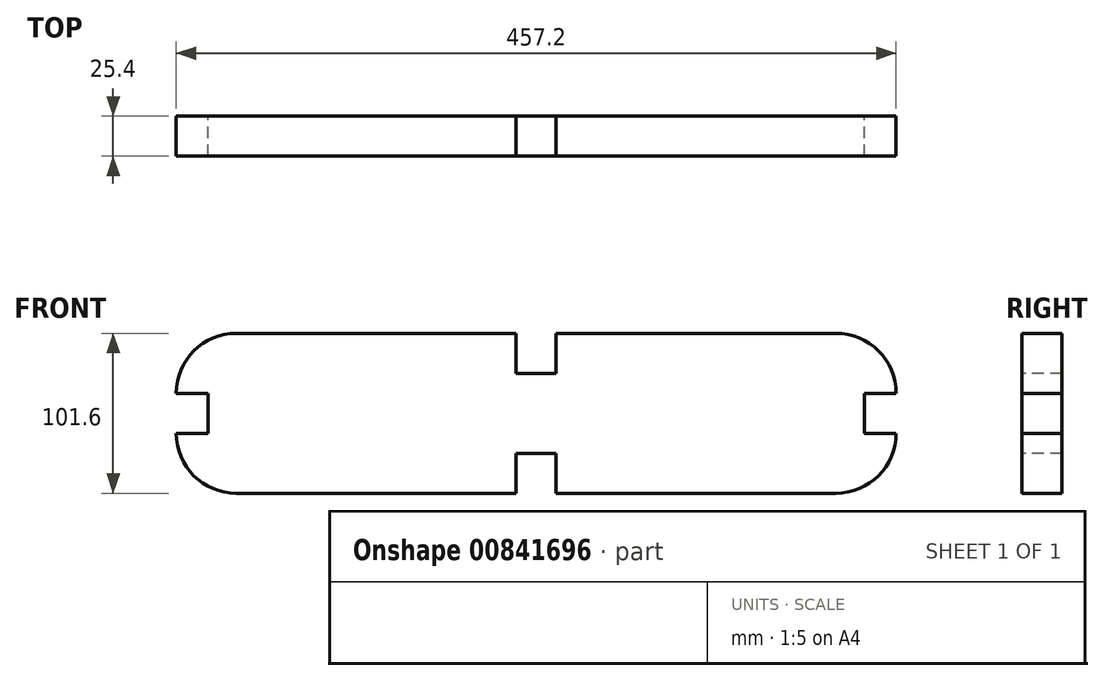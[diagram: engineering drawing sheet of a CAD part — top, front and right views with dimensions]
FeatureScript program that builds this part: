
annotation { "Feature Type Name" : "Feature", "Feature Type Description" : "" }
export const myFeature = defineFeature(function(context is Context, id is Id, definition is map)
    precondition{}
    {
        {
            var Q0;
            Q0=qCreatedBy(makeId("Front.planeOp"),FACE);
            var sketch = newSketch(context, id + "F0", { "sketchPlane" : qUnion([Q0])});
            skLineSegment(sketch, "E0", {"start": v(0, 0) * mm, "end": v(-228.6, 0) * mm, "construction": true});
            skLineSegment(sketch, "E1", {"start": v(0, 0) * mm, "end": v(228.6, 0) * mm, "construction": true});
            skLineSegment(sketch, "E2", {"start": v(0, 0) * mm, "end": v(0, 50.8) * mm, "construction": true});
            skLineSegment(sketch, "E3", {"start": v(0, 0) * mm, "end": v(0, -50.8) * mm, "construction": true});
            skLineSegment(sketch, "E4", {"start": v(0, 50.8) * mm, "end": v(-190.5, 50.8) * mm});
            skLineSegment(sketch, "E5", {"start": v(0, -50.8) * mm, "end": v(-190.5, -50.8) * mm});
            skLineSegment(sketch, "E6", {"start": v(-208.36, 0) * mm, "end": v(-208.36, 12.7) * mm});
            skLineSegment(sketch, "E7", {"start": v(-208.36, 0) * mm, "end": v(-208.36, -12.7) * mm});
            skLineSegment(sketch, "E8", {"start": v(-208.36, 12.7) * mm, "end": v(-228.6, 12.7) * mm});
            skLineSegment(sketch, "E9", {"start": v(-208.36, -12.7) * mm, "end": v(-228.6, -12.7) * mm});
            skLineSegment(sketch, "E10.MirrorCS", {"start": v(0, 50.8) * mm, "end": v(190.5, 50.8) * mm});
            skLineSegment(sketch, "E11.MirrorCS", {"start": v(208.36, 12.7) * mm, "end": v(228.6, 12.7) * mm});
            skLineSegment(sketch, "E12.MirrorCS", {"start": v(208.36, 0) * mm, "end": v(208.36, 12.7) * mm});
            skLineSegment(sketch, "E13.MirrorCS", {"start": v(208.36, 0) * mm, "end": v(208.36, -12.7) * mm});
            skLineSegment(sketch, "E14.MirrorCS", {"start": v(208.36, -12.7) * mm, "end": v(228.6, -12.7) * mm});
            skLineSegment(sketch, "E15.MirrorCS", {"start": v(0, -50.8) * mm, "end": v(190.5, -50.8) * mm});
            skLineSegment(sketch, "E16", {"start": v(-228.6, 12.7) * mm, "end": v(-228.6, 0) * mm, "construction": true});
            skLineSegment(sketch, "E17", {"start": v(-228.6, 0) * mm, "end": v(-228.6, -12.7) * mm, "construction": true});
            skArc(sketch, "E18", {"start": v(-190.5, 50.8) * mm, "mid": v(-217.44, 39.64) * mm, "end": v(-228.6, 12.7) * mm});
            skArc(sketch, "E19", {"start": v(-228.6, -12.7) * mm, "mid": v(-217.44, -39.64) * mm, "end": v(-190.5, -50.8) * mm});
            skArc(sketch, "E20.MirrorCS", {"start": v(190.5, 50.8) * mm, "mid": v(217.44, 39.64) * mm, "end": v(228.6, 12.7) * mm});
            skArc(sketch, "E21.MirrorCS", {"start": v(228.6, -12.7) * mm, "mid": v(217.44, -39.64) * mm, "end": v(190.5, -50.8) * mm});
            skSolve(sketch);
        }
        {
            var Q0;
            Q0 = qSketchRegion(id + "F0", true);
            extrude(context, id + "F1", {"entities" : qUnion([Q0]), "depth" : 25.4 * mm, "offsetDistance" : 25.4 * mm});
        }
        {
            var Q0;
            Q0=makeQuery(id+"F1.opExtrude","CAP_FACE",FACE,{"disambiguationData":[OSD([sQuery(id+"F0.wireOp",EDGE,"E4"),sQuery(id+"F0.wireOp",EDGE,"E5"),sQuery(id+"F0.wireOp",EDGE,"E6"),sQuery(id+"F0.wireOp",EDGE,"E7"),sQuery(id+"F0.wireOp",EDGE,"E8"),sQuery(id+"F0.wireOp",EDGE,"E9"),sQuery(id+"F0.wireOp",EDGE,"E10.MirrorCS"),sQuery(id+"F0.wireOp",EDGE,"E11.MirrorCS"),sQuery(id+"F0.wireOp",EDGE,"E12.MirrorCS"),sQuery(id+"F0.wireOp",EDGE,"E13.MirrorCS"),sQuery(id+"F0.wireOp",EDGE,"E14.MirrorCS"),sQuery(id+"F0.wireOp",EDGE,"E15.MirrorCS"),sQuery(id+"F0.wireOp",EDGE,"E18"),sQuery(id+"F0.wireOp",EDGE,"E19"),sQuery(id+"F0.wireOp",EDGE,"E20.MirrorCS"),sQuery(id+"F0.wireOp",EDGE,"E21.MirrorCS")])],"isStart":false});
            var sketch = newSketch(context, id + "F2", { "sketchPlane" : qUnion([Q0])});
            skLineSegment(sketch, "E22.bottom", {"start": v(-12.7, 50.8) * mm, "end": v(12.7, 50.8) * mm});
            skLineSegment(sketch, "E22.top", {"start": v(-12.7, 25.4) * mm, "end": v(12.7, 25.4) * mm});
            skLineSegment(sketch, "E22.left", {"start": v(-12.7, 50.8) * mm, "end": v(-12.7, 25.4) * mm});
            skLineSegment(sketch, "E22.right", {"start": v(12.7, 50.8) * mm, "end": v(12.7, 25.4) * mm});
            skLineSegment(sketch, "E23", {"start": v(0, 0) * mm, "end": v(0, 25.4) * mm, "construction": true});
            skLineSegment(sketch, "E24.bottom", {"start": v(-12.7, -50.8) * mm, "end": v(12.7, -50.8) * mm});
            skLineSegment(sketch, "E24.top", {"start": v(-12.7, -25.4) * mm, "end": v(12.7, -25.4) * mm});
            skLineSegment(sketch, "E24.left", {"start": v(-12.7, -50.8) * mm, "end": v(-12.7, -25.4) * mm});
            skLineSegment(sketch, "E24.right", {"start": v(12.7, -50.8) * mm, "end": v(12.7, -25.4) * mm});
            skLineSegment(sketch, "E25", {"start": v(0, 0) * mm, "end": v(0, -25.4) * mm});
            skSolve(sketch);
        }
        {
            var Q0;
            Q0=makeQuery(id+"F2.imprint","IMPRINT",FACE,{"disambiguationData":[TD([[makeQuery(id+"F2.imprint","IMPRINT",EDGE,{"derivedFrom":sQuery(id+"F2.wireOp",EDGE,"E22.bottom")}),-1.0]])]});
            var Q1;
            Q1=makeQuery(id+"F2.imprint","IMPRINT",FACE,{"disambiguationData":[TD([[makeQuery(id+"F2.imprint","IMPRINT",EDGE,{"derivedFrom":sQuery(id+"F2.wireOp",EDGE,"E24.bottom")}),-1.0]])]});
            extrude(context, id + "F3", {"entities" : qUnion([Q0, Q1]), "operationType" : NewBodyOperationType.REMOVE, "oppositeDirection" : true, "depth" : 25.4 * mm, "offsetDistance" : 25.4 * mm});
        }
    });
